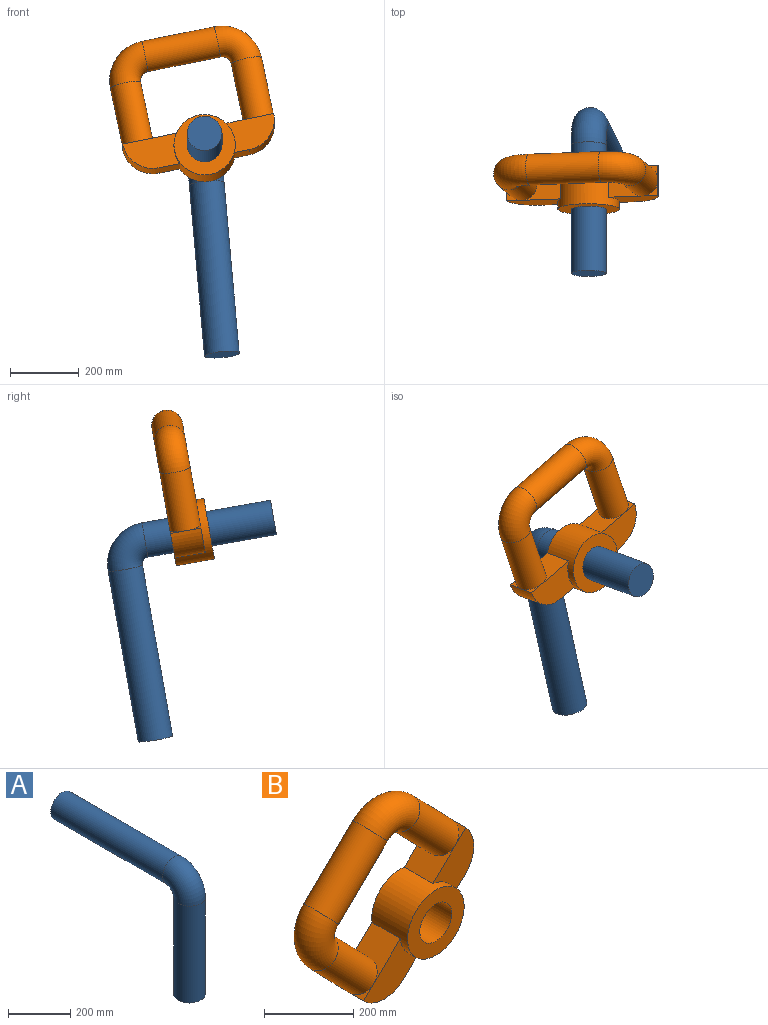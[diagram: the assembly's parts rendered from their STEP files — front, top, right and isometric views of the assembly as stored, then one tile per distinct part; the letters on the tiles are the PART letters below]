
ASSEMBLY  parts=2 mates=1
PART A: 5 faces, bbox 101.6x639.4x512.4 mm
  f0: torus R=70.58mm, axis (-1,0,0), area 35388.1mm2, adj f1,f3
  f1: cylinder r=50.8mm len=508mm, axis (0,-1,0), area 162146.4mm2, adj f0,f2
  f2: plane 101.6x101.6mm, normal (0,1,0), area 8107.3mm2, adj f1
  f3: cylinder r=50.8mm len=381mm, axis (0,0,1), area 121609.8mm2, adj f0,f4
  f4: plane 101.6x101.6mm, normal (0,0,-1), area 8107.3mm2, adj f3
PART B: 21 faces, bbox 514.6x113.5x513.2 mm
  f0: plane 90x32.48mm, normal (0.7,0,-0.72), area 4071.6mm2, adj f4,f5,f8,f18
  f1: plane 90x72.23mm, normal (-0.7,0,0.72), area 5874.4mm2, adj f4,f5,f10,f18
  f2: plane 90x44.02mm, normal (0.7,0,-0.72), area 5518mm2, adj f5,f12,f15,f18
  f3: plane 90x83.77mm, normal (-0.7,0,0.72), area 7320.8mm2, adj f5,f12,f17,f18
  f4: plane 158.76x129.93mm, normal (0,-1,0), area 10146.2mm2, adj f0,f1,f8,f9,f18
  f5: plane 348.71x340.86mm, normal (0,1,0), area 38815.3mm2, adj f0,f1,f2,f3,f7,f8,f14,f15
  f6: torus R=72.18mm, axis (0,1,0), area 32059.3mm2, adj f10,f11
  f7: plane 45x32.31mm, normal (-0.7,0,0.72), area 434.6mm2, adj f5,f8,f10
  f8: cylinder r=90mm len=127.26mm, axis (0,1,0), area 12723.5mm2, adj f0,f4,f5,f7,f9
  f9: plane 45x32.31mm, normal (-0.7,0,0.72), area 434.6mm2, adj f4,f8,f10
  f10: cylinder r=45mm len=189.72mm, axis (0.7,0,-0.72), area 50045.6mm2, adj f1,f6,f7,f9
  f11: cylinder r=45mm len=217.72mm, axis (0.72,0,0.7), area 61072.6mm2, adj f6,f13
  f12: plane 171.28x139.9mm, normal (0,-1,0), area 11592.5mm2, adj f2,f3,f15,f16,f18
  f13: torus R=72.18mm, axis (0,1,0), area 32059.3mm2, adj f11,f17
  f14: plane 45x32.31mm, normal (-0.7,0,0.72), area 434.6mm2, adj f5,f15,f17
  f15: cylinder r=90mm len=127.26mm, axis (0,1,0), area 12723.5mm2, adj f2,f5,f12,f14,f16
  f16: plane 45x32.31mm, normal (-0.7,0,0.72), area 434.6mm2, adj f12,f15,f17
  f17: cylinder r=45mm len=189.72mm, axis (0.7,0,-0.72), area 50045.6mm2, adj f3,f13,f14,f16
  f18: cylinder r=89.53mm len=179.07mm, axis (0,1,0), area 46773.6mm2, adj f0,f1,f2,f3,f4,f5,f12,f20
  f19: cylinder r=50.8mm len=113.54mm, axis (0,1,0), area 36239.7mm2, adj f5,f20
  f20: plane 179.07x179.07mm, normal (0,-1,0), area 17076.6mm2, adj f18,f19
PLACE A rot(axis=(-1,-0.04,-0.04),100.1deg) t=(-661.51,156.76,548.11)mm fixed
PLACE B rot(axis=(-0.29,0.95,-0.08),34deg) t=(-648.41,51.82,639.72)mm
MATE revolute A.f3 <-> B.f19  axis (0,0.98,-0.17) through (-648.41,-59.99,659.44)mm
